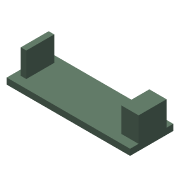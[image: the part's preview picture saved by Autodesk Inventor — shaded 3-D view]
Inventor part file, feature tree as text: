
AUTODESK INVENTOR PART (.ipt)
format: ipt  version: 2019.4 (Build 234330000, 330)  size: 86,528 bytes
history: native  units: mm
features: extrude x2, sketch x2
ambient origin geometry x8: Origin, YZ Plane, XZ Plane, XY Plane, X Axis, Y Axis, Z Axis, Center Point
bodies: Solid1 (feature_tree)
feature tree (4):
  extrude  "Extrusion1"  Depth=14.0mm
  extrude  "Extrusion2"  Depth=8.0mm TaperAngle=0.0deg
  sketch  "Sketch1"  dims[d0=40.0mm d1=14.0mm]
  sketch  "Sketch2"  dims[d2=2.0mm d3=0.0mm d4=8.0mm d5=0.0mm]
